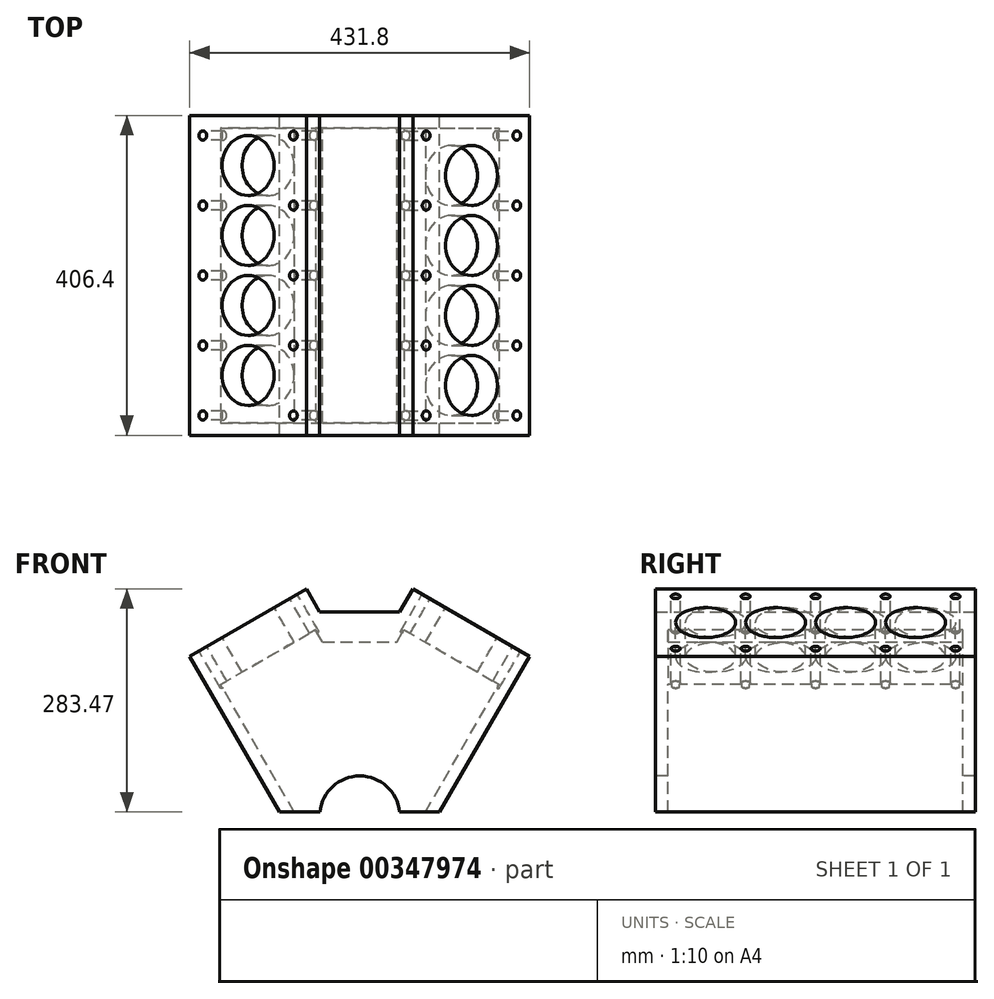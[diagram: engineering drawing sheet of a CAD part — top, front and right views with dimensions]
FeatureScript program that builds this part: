
annotation { "Feature Type Name" : "Feature", "Feature Type Description" : "" }
export const myFeature = defineFeature(function(context is Context, id is Id, definition is map)
    precondition{}
    {
        {
            var Q0;
            Q0=qCreatedBy(makeId("Front.planeOp"),FACE);
            var sketch = newSketch(context, id + "F0", { "sketchPlane" : qUnion([Q0])});
            skLineSegment(sketch, "E0", {"start": v(-215.9, -56.03) * mm, "end": v(-101.6, -254) * mm});
            skLineSegment(sketch, "E1", {"start": v(-101.6, -254) * mm, "end": v(101.6, -254) * mm});
            skLineSegment(sketch, "E2", {"start": v(101.6, -254) * mm, "end": v(215.9, -56.03) * mm});
            skLineSegment(sketch, "E3", {"start": v(215.9, -56.03) * mm, "end": v(67.81, 29.47) * mm});
            skLineSegment(sketch, "E4", {"start": v(67.81, 29.47) * mm, "end": v(50.8, 0) * mm});
            skLineSegment(sketch, "E5", {"start": v(50.8, 0) * mm, "end": v(-50.8, 0) * mm});
            skLineSegment(sketch, "E6", {"start": v(-50.8, 0) * mm, "end": v(-67.81, 29.47) * mm});
            skLineSegment(sketch, "E7", {"start": v(-67.81, 29.47) * mm, "end": v(-215.9, -56.03) * mm});
            skLineSegment(sketch, "E8", {"start": v(0, 0) * mm, "end": v(0, -254) * mm, "construction": true});
            skSolve(sketch);
        }
        {
            var Q0;
            Q0 = qSketchRegion(id + "F0", true);
            extrude(context, id + "F1", {"entities" : qUnion([Q0]), "depth" : 406.4 * mm});
        }
        {
            var Q0;
            Q0=makeQuery(id+"F1.opExtrude","SWEPT_FACE",FACE,{"disambiguationData":[OSD([sQuery(id+"F0.wireOp",EDGE,"E3")])]});
            var sketch = newSketch(context, id + "F2", { "sketchPlane" : qUnion([Q0])});
            skCircle(sketch, "E9", {"center": v(129.5, -76.2) * mm, "radius": 38.1 * mm});
            skCircle(sketch, "E10", {"center": v(129.5, -165.1) * mm, "radius": 38.1 * mm});
            skCircle(sketch, "E11", {"center": v(129.5, -254) * mm, "radius": 38.1 * mm});
            skCircle(sketch, "E12", {"center": v(129.5, -342.9) * mm, "radius": 38.1 * mm});
            skSolve(sketch);
        }
        {
            var Q0;
            Q0 = qSketchRegion(id + "F2", true);
            extrude(context, id + "F3", {"entities" : qUnion([Q0]), "operationType" : NewBodyOperationType.REMOVE, "endBound" : BoundingType.THROUGH_ALL, "oppositeDirection" : true, "depth" : 25.4 * mm});
        }
        {
            var Q0;
            Q0=makeQuery(id+"F1.opExtrude","SWEPT_FACE",FACE,{"disambiguationData":[OSD([sQuery(id+"F0.wireOp",EDGE,"E7")])]});
            var sketch = newSketch(context, id + "F4", { "sketchPlane" : qUnion([Q0])});
            skCircle(sketch, "E13", {"center": v(-129.5, -63.5) * mm, "radius": 38.1 * mm});
            skCircle(sketch, "E14", {"center": v(-129.5, -152.4) * mm, "radius": 38.1 * mm});
            skCircle(sketch, "E15", {"center": v(-129.5, -241.3) * mm, "radius": 38.1 * mm});
            skCircle(sketch, "E16", {"center": v(-129.5, -330.2) * mm, "radius": 38.1 * mm});
            skSolve(sketch);
        }
        {
            var Q0;
            Q0 = qSketchRegion(id + "F4", true);
            extrude(context, id + "F5", {"entities" : qUnion([Q0]), "operationType" : NewBodyOperationType.REMOVE, "endBound" : BoundingType.THROUGH_ALL, "oppositeDirection" : true, "depth" : 25.4 * mm});
        }
        {
            var Q0;
            Q0=makeQuery(id+"F1.opExtrude","SWEPT_FACE",FACE,{"disambiguationData":[OSD([sQuery(id+"F0.wireOp",EDGE,"E3")])]});
            cPlane(context, id + "F6", {"entities" : qUnion([Q0]), "cplaneType" : CPlaneType.OFFSET, "offset" : 50.8 * mm, "oppositeDirection" : true, "width" : 152.4 * mm, "height" : 152.4 * mm});
        }
        {
            var Q0;
            Q0=makeQuery(id+"F1.opExtrude","SWEPT_FACE",FACE,{"disambiguationData":[OSD([sQuery(id+"F0.wireOp",EDGE,"E7")])]});
            cPlane(context, id + "F7", {"entities" : qUnion([Q0]), "cplaneType" : CPlaneType.OFFSET, "offset" : 50.8 * mm, "oppositeDirection" : true, "width" : 152.4 * mm, "height" : 152.4 * mm});
        }
        {
            var Q0;
            Q0=qCreatedBy(id+"F6.planeOp",FACE);
            var sketch = newSketch(context, id + "F8", { "sketchPlane" : qUnion([Q0])});
            skLineSegment(sketch, "E17.bottom", {"start": v(59.87, -15.88) * mm, "end": v(199.11, -15.88) * mm});
            skLineSegment(sketch, "E17.top", {"start": v(59.87, -390.53) * mm, "end": v(199.11, -390.53) * mm});
            skLineSegment(sketch, "E17.left", {"start": v(59.87, -15.88) * mm, "end": v(59.87, -390.53) * mm});
            skLineSegment(sketch, "E17.right", {"start": v(199.11, -15.88) * mm, "end": v(199.11, -390.53) * mm});
            skSolve(sketch);
        }
        {
            var Q0;
            Q0 = qSketchRegion(id + "F8", true);
            extrude(context, id + "F9", {"entities" : qUnion([Q0]), "operationType" : NewBodyOperationType.REMOVE, "endBound" : BoundingType.THROUGH_ALL, "oppositeDirection" : true, "depth" : 25.4 * mm});
        }
        {
            var Q0;
            Q0=qCreatedBy(id+"F7.planeOp",FACE);
            var sketch = newSketch(context, id + "F10", { "sketchPlane" : qUnion([Q0])});
            skLineSegment(sketch, "E18.bottom", {"start": v(-199.11, -15.88) * mm, "end": v(-59.87, -15.88) * mm});
            skLineSegment(sketch, "E18.top", {"start": v(-199.11, -390.53) * mm, "end": v(-59.87, -390.53) * mm});
            skLineSegment(sketch, "E18.left", {"start": v(-199.11, -15.88) * mm, "end": v(-199.11, -390.53) * mm});
            skLineSegment(sketch, "E18.right", {"start": v(-59.87, -15.87) * mm, "end": v(-59.87, -390.53) * mm});
            skSolve(sketch);
        }
        {
            var Q0;
            Q0 = qSketchRegion(id + "F10", true);
            extrude(context, id + "F11", {"entities" : qUnion([Q0]), "operationType" : NewBodyOperationType.REMOVE, "endBound" : BoundingType.THROUGH_ALL, "oppositeDirection" : true, "depth" : 25.4 * mm});
        }
        {
            var Q0;
            Q0=makeQuery(id+"F1.opExtrude","CAP_FACE",FACE,{"disambiguationData":[OSD([sQuery(id+"F0.wireOp",EDGE,"E0"),sQuery(id+"F0.wireOp",EDGE,"E1"),sQuery(id+"F0.wireOp",EDGE,"E2"),sQuery(id+"F0.wireOp",EDGE,"E3"),sQuery(id+"F0.wireOp",EDGE,"E4"),sQuery(id+"F0.wireOp",EDGE,"E5"),sQuery(id+"F0.wireOp",EDGE,"E6"),sQuery(id+"F0.wireOp",EDGE,"E7")])],"isStart":false});
            var sketch = newSketch(context, id + "F12", { "sketchPlane" : qUnion([Q0])});
            skLineSegment(sketch, "E19", {"start": v(-141.86, -13.28) * mm, "end": v(0, -258.98) * mm, "construction": true});
            skLineSegment(sketch, "E20", {"start": v(0, -258.98) * mm, "end": v(141.86, -13.28) * mm, "construction": true});
            skCircle(sketch, "E21", {"center": v(0, -258.98) * mm, "radius": 50.8 * mm});
            skSolve(sketch);
        }
        {
            var Q0;
            Q0 = qSketchRegion(id + "F12", true);
            extrude(context, id + "F13", {"entities" : qUnion([Q0]), "operationType" : NewBodyOperationType.REMOVE, "endBound" : BoundingType.THROUGH_ALL, "oppositeDirection" : true, "depth" : 25.4 * mm});
        }
        {
            var Q0;
            Q0=makeQuery(id+"F1.opExtrude","SWEPT_FACE",FACE,{"disambiguationData":[OSD([sQuery(id+"F0.wireOp",EDGE,"E5")])]});
            cPlane(context, id + "F14", {"entities" : qUnion([Q0]), "cplaneType" : CPlaneType.OFFSET, "offset" : 38.1 * mm, "oppositeDirection" : true, "width" : 152.4 * mm, "height" : 152.4 * mm});
        }
        {
            var Q0;
            Q0=qCreatedBy(id+"F14.planeOp",FACE);
            var sketch = newSketch(context, id + "F15", { "sketchPlane" : qUnion([Q0])});
            skLineSegment(sketch, "E22.bottom", {"start": v(-56.16, -15.88) * mm, "end": v(56.16, -15.87) * mm});
            skLineSegment(sketch, "E22.top", {"start": v(-56.16, -390.53) * mm, "end": v(56.16, -390.53) * mm});
            skLineSegment(sketch, "E22.left", {"start": v(-56.16, -15.88) * mm, "end": v(-56.16, -390.53) * mm});
            skLineSegment(sketch, "E22.right", {"start": v(56.16, -15.88) * mm, "end": v(56.16, -390.53) * mm});
            skSolve(sketch);
        }
        {
            var Q0;
            Q0 = qSketchRegion(id + "F15", true);
            extrude(context, id + "F16", {"entities" : qUnion([Q0]), "operationType" : NewBodyOperationType.REMOVE, "endBound" : BoundingType.THROUGH_ALL, "oppositeDirection" : true, "depth" : 25.4 * mm});
        }
        {
            var Q0;
            Q0=makeQuery(id+"F1.opExtrude","SWEPT_FACE",FACE,{"disambiguationData":[OSD([sQuery(id+"F0.wireOp",EDGE,"E3")])]});
            var sketch = newSketch(context, id + "F17", { "sketchPlane" : qUnion([Q0])});
            skPoint(sketch, "E23", {"position": v(63.04, -381) * mm});
            skPoint(sketch, "E24", {"position": v(195.94, -381) * mm});
            skPoint(sketch, "E25", {"position": v(195.94, -292.1) * mm});
            skPoint(sketch, "E26", {"position": v(195.94, -203.2) * mm});
            skPoint(sketch, "E27", {"position": v(195.94, -25.4) * mm});
            skPoint(sketch, "E28", {"position": v(63.04, -25.4) * mm});
            skPoint(sketch, "E29", {"position": v(63.04, -292.1) * mm});
            skPoint(sketch, "E30", {"position": v(63.04, -203.2) * mm});
            skPoint(sketch, "E31", {"position": v(63.04, -114.3) * mm});
            skPoint(sketch, "E32", {"position": v(195.94, -114.3) * mm});
            skSolve(sketch);
        }
        {
            var Q0;
            Q0=makeQuery(id+"F1.opExtrude","SWEPT_FACE",FACE,{"disambiguationData":[OSD([sQuery(id+"F0.wireOp",EDGE,"E7")])]});
            var sketch = newSketch(context, id + "F18", { "sketchPlane" : qUnion([Q0])});
            skPoint(sketch, "E33", {"position": v(-195.94, -381) * mm});
            skPoint(sketch, "E34", {"position": v(-63.04, -381) * mm});
            skPoint(sketch, "E35", {"position": v(-63.04, -292.1) * mm});
            skPoint(sketch, "E36", {"position": v(-63.04, -203.2) * mm});
            skPoint(sketch, "E37", {"position": v(-63.04, -114.3) * mm});
            skPoint(sketch, "E38", {"position": v(-63.04, -25.4) * mm});
            skPoint(sketch, "E39", {"position": v(-195.94, -25.4) * mm});
            skPoint(sketch, "E40", {"position": v(-195.94, -114.3) * mm});
            skPoint(sketch, "E41", {"position": v(-195.94, -203.2) * mm});
            skPoint(sketch, "E42", {"position": v(-195.94, -292.1) * mm});
            skSolve(sketch);
        }
        {
            var Q0;
            Q0=sQuery(id+"F18.wireOp",VERTEX,"E33");
            var Q1;
            Q1=sQuery(id+"F18.wireOp",VERTEX,"E34");
            var Q2;
            Q2=sQuery(id+"F18.wireOp",VERTEX,"E35");
            var Q3;
            Q3=sQuery(id+"F18.wireOp",VERTEX,"E42");
            var Q4;
            Q4=sQuery(id+"F18.wireOp",VERTEX,"E41");
            var Q5;
            Q5=sQuery(id+"F18.wireOp",VERTEX,"E36");
            var Q6;
            Q6=sQuery(id+"F18.wireOp",VERTEX,"E37");
            var Q7;
            Q7=sQuery(id+"F18.wireOp",VERTEX,"E40");
            var Q8;
            Q8=sQuery(id+"F18.wireOp",VERTEX,"E39");
            var Q9;
            Q9=sQuery(id+"F18.wireOp",VERTEX,"E38");
            var Q10;
            Q10=sQuery(id+"F17.wireOp",VERTEX,"E28");
            var Q11;
            Q11=sQuery(id+"F17.wireOp",VERTEX,"E31");
            var Q12;
            Q12=sQuery(id+"F17.wireOp",VERTEX,"E30");
            var Q13;
            Q13=sQuery(id+"F17.wireOp",VERTEX,"E29");
            var Q14;
            Q14=sQuery(id+"F17.wireOp",VERTEX,"E23");
            var Q15;
            Q15=sQuery(id+"F17.wireOp",VERTEX,"E24");
            var Q16;
            Q16=sQuery(id+"F17.wireOp",VERTEX,"E25");
            var Q17;
            Q17=sQuery(id+"F17.wireOp",VERTEX,"E26");
            var Q18;
            Q18=sQuery(id+"F17.wireOp",VERTEX,"E32");
            var Q19;
            Q19=sQuery(id+"F17.wireOp",VERTEX,"E27");
            var Q20;
            Q20=makeQuery(id+"F1.opExtrude","SWEPT_BODY",BODY,{"disambiguationData":[OSD([sQuery(id+"F0.wireOp",EDGE,"E0"),sQuery(id+"F0.wireOp",EDGE,"E1"),sQuery(id+"F0.wireOp",EDGE,"E2"),sQuery(id+"F0.wireOp",EDGE,"E3"),sQuery(id+"F0.wireOp",EDGE,"E4"),sQuery(id+"F0.wireOp",EDGE,"E5"),sQuery(id+"F0.wireOp",EDGE,"E6"),sQuery(id+"F0.wireOp",EDGE,"E7")])]});
            hole(context, id + "F19", {"style" : HoleStyle.SIMPLE, "endStyle" : HoleEndStyle.BLIND, "standardTappedOrClearance" : lookupTablePath({ "standard" : "ANSI", "engagement" : "75%", "pitch" : "20 tpi", "size" : "1/2", "type" : "Tapped" }), "standardBlindInLast" : lookupTablePath({ "standard" : "ANSI", "engagement" : "75%", "pitch" : "20 tpi", "size" : "1/2", "type" : "Tapped" }), "holeDiameter" : 11.5 * mm, "showTappedDepth" : true, "holeDepth" : 54.6 * mm, "tappedDepth" : 50.8 * mm, "tapClearance" : 3, "locations" : qUnion([Q0, Q1, Q2, Q3, Q4, Q5, Q6, Q7, Q8, Q9, Q10, Q11, Q12, Q13, Q14, Q15, Q16, Q17, Q18, Q19]), "scope" : qUnion([Q20]), "majorDiameter" : 12.7 * mm});
        }
    });
